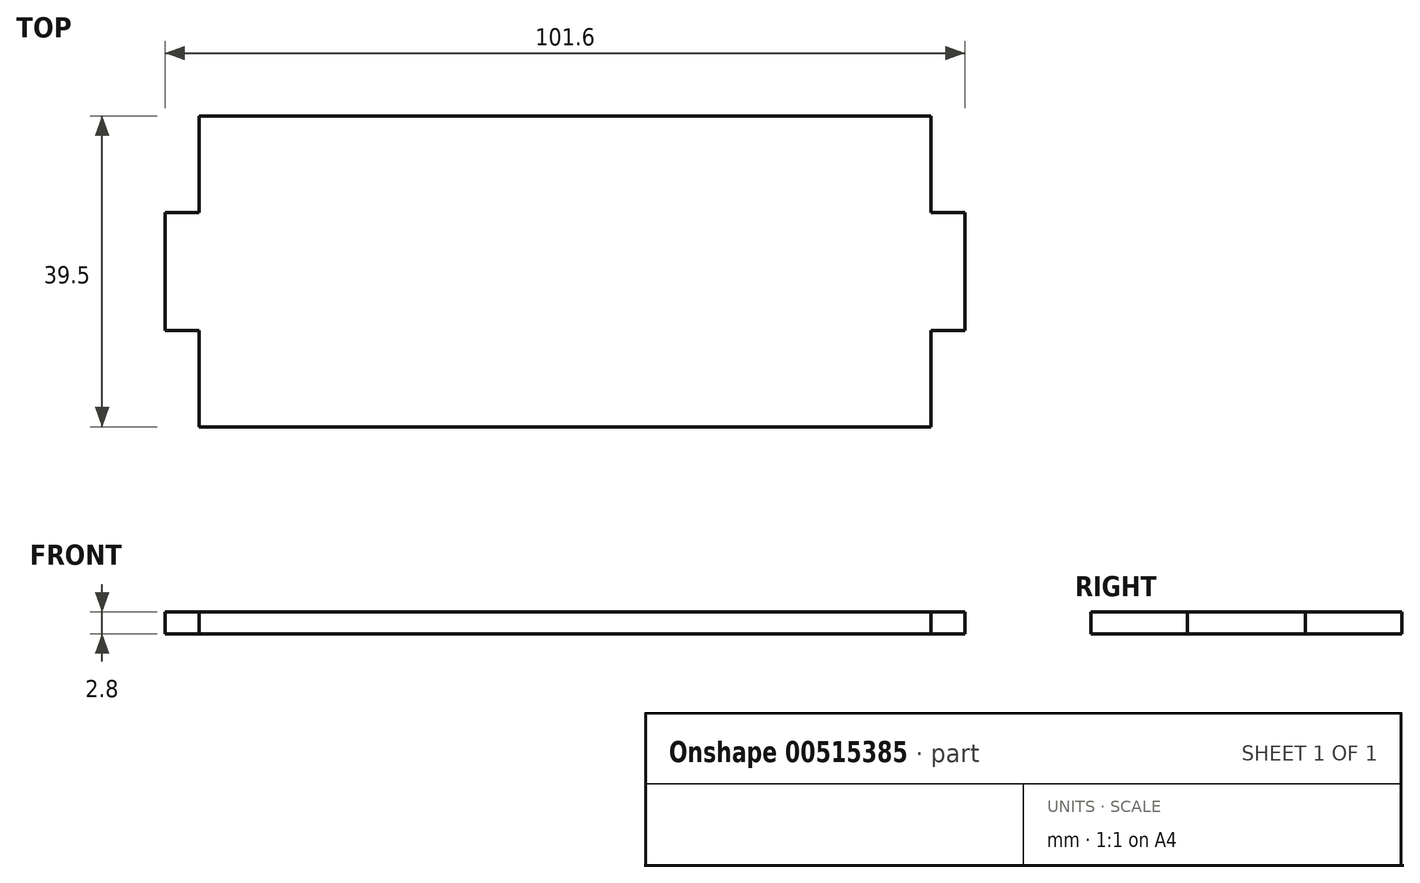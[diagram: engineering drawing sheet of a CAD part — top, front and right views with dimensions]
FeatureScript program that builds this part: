
annotation { "Feature Type Name" : "Feature", "Feature Type Description" : "" }
export const myFeature = defineFeature(function(context is Context, id is Id, definition is map)
    precondition{}
    {
        {
            var Q0;
            Q0=qCreatedBy(makeId("Top.planeOp"),FACE);
            var sketch = newSketch(context, id + "F0", { "sketchPlane" : qUnion([Q0])});
            skLineSegment(sketch, "E0.bottom", {"start": v(46.5, 19.75) * mm, "end": v(-46.5, 19.75) * mm});
            skLineSegment(sketch, "E0.top", {"start": v(46.5, -19.75) * mm, "end": v(-46.5, -19.75) * mm});
            skLineSegment(sketch, "E0.left", {"start": v(46.5, 19.75) * mm, "end": v(46.5, -19.75) * mm});
            skLineSegment(sketch, "E0.right", {"start": v(-46.5, 19.75) * mm, "end": v(-46.5, -19.75) * mm});
            skPoint(sketch, "E0.middle", {"position": v(0, 0) * mm});
            skLineSegment(sketch, "E1.bottom", {"start": v(50.8, 7.5) * mm, "end": v(-50.8, 7.5) * mm});
            skLineSegment(sketch, "E1.top", {"start": v(50.8, -7.5) * mm, "end": v(-50.8, -7.5) * mm});
            skLineSegment(sketch, "E1.left", {"start": v(50.8, 7.5) * mm, "end": v(50.8, -7.5) * mm});
            skLineSegment(sketch, "E1.right", {"start": v(-50.8, 7.5) * mm, "end": v(-50.8, -7.5) * mm});
            skSolve(sketch);
        }
        {
            var Q0;
            {var subQ0=sQuery(id+"F0.wireOp",EDGE,"E1.bottom");var subQ1=sQuery(id+"F0.wireOp",EDGE,"E0.left");var subQ2=makeQuery(id+"F0.imprint","INTERSECT",VERTEX,{"derivedFrom":[subQ1,subQ0]});Q0=makeQuery(id+"F0.imprint","IMPRINT",FACE,{"disambiguationData":[TD([[makeQuery(id+"F0.imprint","IMPRINT",EDGE,{"disambiguationData":[TD([[subQ2,-1.0]])],"derivedFrom":subQ1}),-1.0]])]});}
            var Q1;
            {var subQ5=sQuery(id+"F0.wireOp",EDGE,"E1.right");Q1=makeQuery(id+"F0.imprint","IMPRINT",FACE,{"disambiguationData":[TD([[makeQuery(id+"F0.imprint","IMPRINT",EDGE,{"derivedFrom":subQ5}),1.0]])]});}
            var Q2;
            {var subQ0=sQuery(id+"F0.wireOp",EDGE,"E0.bottom");Q2=makeQuery(id+"F0.imprint","IMPRINT",FACE,{"disambiguationData":[TD([[makeQuery(id+"F0.imprint","IMPRINT",EDGE,{"derivedFrom":subQ0}),1.0]])]});}
            var Q3;
            {var subQ0=sQuery(id+"F0.wireOp",EDGE,"E0.top");Q3=makeQuery(id+"F0.imprint","IMPRINT",FACE,{"disambiguationData":[TD([[makeQuery(id+"F0.imprint","IMPRINT",EDGE,{"derivedFrom":subQ0}),-1.0]])]});}
            var Q4;
            {var subQ5=sQuery(id+"F0.wireOp",EDGE,"E1.left");Q4=makeQuery(id+"F0.imprint","IMPRINT",FACE,{"disambiguationData":[TD([[makeQuery(id+"F0.imprint","IMPRINT",EDGE,{"derivedFrom":subQ5}),-1.0]])]});}
            extrude(context, id + "F1", {"entities" : qUnion([Q0, Q1, Q2, Q3, Q4]), "depth" : 2.8 * mm, "offsetDistance" : 25.4 * mm, "symmetric" : true});
        }
    });
